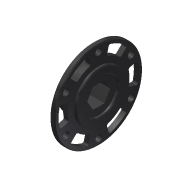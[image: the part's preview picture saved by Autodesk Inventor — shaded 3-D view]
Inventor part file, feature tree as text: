
AUTODESK INVENTOR PART (.ipt)
format: ipt  version: 2015 (Build 190159000, 159)  size: 236,544 bytes
history: native  units: in
note: dims shown in document units (in); Inventor stores cm internally (conversion verified against a paired STEP export)
features: imported_body x2, sketch x2, extrude x1, hole x1, pattern_circular x1
ambient origin geometry x8: Origin, YZ Plane, XZ Plane, XY Plane, X Axis, Y Axis, Z Axis, Center Point
bodies: Body1 (feature_tree)
feature tree (7):
  imported_body  "Imported1"
  extrude  "Extrusion1"  Depth=0.9375in
  hole  "Hole1"  [1 undecoded]
  pattern_circular  "Circular Pattern1"  [2 undecoded]
  imported_body  "Base1"
  sketch  "Sketch1"  dims[d0=1.0in d1=0.0in d2=0.9375in]
  sketch  "Sketch2"  dims[d3=0.169in d4=0.75in d5=0.375in d6=0.25in d7=0.5635in d8=1.0in d9=0.8108in d10=2.3622in d11=360.0deg]
note: 3 required parameter values undecoded (feature->parameter linkage not recoverable at this tier; creation-order binding heuristic only, values carry confidence <= 0.55)
